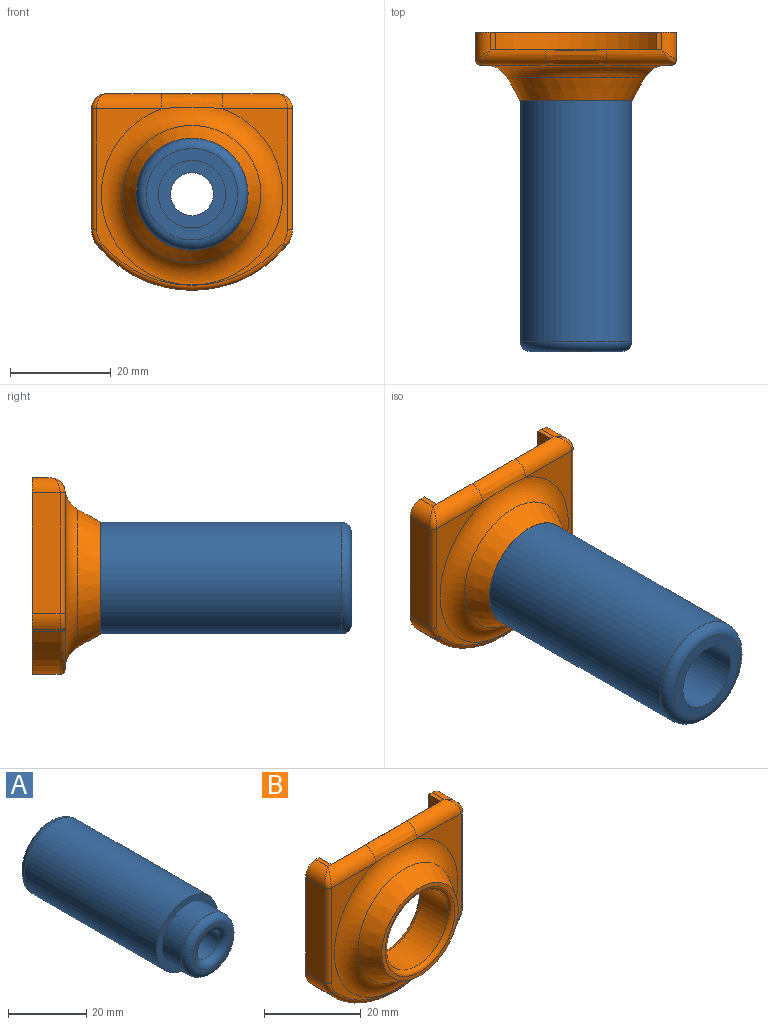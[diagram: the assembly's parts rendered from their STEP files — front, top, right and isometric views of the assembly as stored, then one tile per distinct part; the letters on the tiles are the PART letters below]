
ASSEMBLY  parts=2 mates=1
PART A: 11 faces, bbox 24x59x24 mm
  f0: cylinder r=11.1mm len=48mm, axis (0,-1,0), area 3347.7mm2, adj f7,f10
  f1: plane 14.2x14.2mm, normal (0,-1,0), area 35.6mm2, adj f8,f9
  f2: cylinder r=6.7mm len=34mm, axis (0,-1,0), area 1431.3mm2, adj f3,f4
  f3: plane 18.2x18.2mm, normal (0,1,0), area 119.1mm2, adj f2,f10
  f4: plane 13.4x13.4mm, normal (0,1,0), area 84.3mm2, adj f2,f5
  f5: cylinder r=4.25mm len=23mm, axis (0,1,0), area 614.2mm2, adj f4,f9
  f6: cylinder r=9.1mm len=18.2mm, axis (0,-1,0), area 400.2mm2, adj f7,f8
  f7: plane 22.2x22.2mm, normal (0,-1,0), area 126.9mm2, adj f0,f6
  f8: torus R=7.1mm, axis (0,-1,0), area 165.3mm2, adj f1,f6
  f9: torus R=6.25mm, axis (0,-1,0), area 98.2mm2, adj f1,f5
  f10: torus R=9.1mm, axis (0,-1,0), area 204.8mm2, adj f0,f3
PART B: 46 faces, bbox 46.7x13.5x46.7 mm
  f0: plane 40x39.13mm, normal (0,1,0), area 362.7mm2, adj f1,f4,f5,f6,f7,f8,f9,f10
  f1: plane 3.5x1mm, normal (0,0,1), area 3.5mm2, adj f0,f12,f28,f30
  f2: plane 12.11x0.07mm, normal (0,0,1), area 0.4mm2, adj f15,f31
  f3: plane 22.33x22.33mm, normal (0,-1,0), area 64.6mm2, adj f17,f45
  f4: plane 24.05x5.5mm, normal (1,0,0), area 132.3mm2, adj f0,f10,f25,f34
  f5: plane 24.05x5.5mm, normal (-1,0,0), area 132.3mm2, adj f0,f8,f19,f28
  f6: plane 5.5x0.3mm, normal (-0.76,0,-0.65), area 2.2mm2, adj f0,f8,f9,f21
  f7: plane 5.5x0.3mm, normal (0.76,0,-0.65), area 2.2mm2, adj f0,f9,f10,f23
  f8: cylinder r=5mm len=5.5mm, axis (0,1,0), area 19.5mm2, adj f0,f5,f6,f20
  f9: cylinder r=24.42mm len=37.07mm, axis (0,1,0), area 231.5mm2, adj f0,f6,f7,f22
  f10: cylinder r=5mm len=5.5mm, axis (0,1,0), area 19.5mm2, adj f0,f4,f7,f24
  f11: cylinder r=9.2mm len=18.4mm, axis (0,1,0), area 462.4mm2, adj f26,f45
  f12: plane 27.39x3.5mm, normal (1,0,0), area 95.9mm2, adj f0,f1,f13,f15
  f13: cylinder r=20.42mm len=32mm, axis (0,-1,0), area 128.7mm2, adj f0,f12,f14,f15
  f14: plane 27.39x3.5mm, normal (-1,0,0), area 95.9mm2, adj f0,f13,f15,f27
  f15: plane 35.13x32mm, normal (0,1,0), area 722.2mm2, adj f2,f12,f13,f14,f26,f30,f32
  f16: plane 38x35.13mm, normal (0,-1,0), area 209.1mm2, adj f18,f19,f20,f21,f22,f23,f24,f25
  f17: cone r=15.12mm half-angle=29.6deg, axis (0,1,0), area 401.1mm2, adj f3,f18
  f18: torus R=18.05mm, axis (0,-1,0), area 513.1mm2, adj f16,f17,f31
  f19: cylinder r=1mm len=24.05mm, axis (0,0,1), area 37.8mm2, adj f5,f16,f20,f29
  f20: torus R=4mm, axis (0,-1,0), area 5.2mm2, adj f8,f16,f19,f21
  f21: cylinder r=1mm len=1.02mm, axis (-0.65,0,0.76), area 0.6mm2, adj f6,f16,f20,f22
  f22: torus R=23.42mm, axis (0,-1,0), area 65.1mm2, adj f9,f16,f21,f23
  f23: cylinder r=1mm len=1.02mm, axis (-0.65,0,-0.76), area 0.6mm2, adj f7,f16,f22,f24
  f24: torus R=4mm, axis (0,-1,0), area 5.2mm2, adj f10,f16,f23,f25
  f25: cylinder r=1mm len=24.05mm, axis (0,0,-1), area 37.8mm2, adj f4,f16,f24,f33
  f26: torus R=10.2mm, axis (0,-1,0), area 94.4mm2, adj f11,f15
  f27: plane 3.5x1mm, normal (0,0,1), area 3.5mm2, adj f0,f14,f32,f34
  f28: cylinder r=3mm len=5.5mm, axis (0,1,0), area 22.5mm2, adj f0,f1,f5,f29
  f29: bspline ~3.52x3mm, area 5mm2, adj f19,f28,f30
  f30: cylinder r=3mm len=12.95mm, axis (-1,0,0), area 57.6mm2, adj f1,f15,f16,f29,f31
  f31: bspline ~16.45x3.42mm, area 53.9mm2, adj f2,f18,f30,f32
  f32: cylinder r=3mm len=12.95mm, axis (-1,0,0), area 57.6mm2, adj f15,f16,f27,f31,f33
  f33: bspline ~3.52x3mm, area 5mm2, adj f25,f32,f34
  f34: cylinder r=3mm len=5.5mm, axis (0,-1,0), area 22.5mm2, adj f0,f4,f27,f33
  f35: cylinder r=1.25mm len=4mm, axis (0,1,0), area 31.4mm2, adj f0,f36
  f36: plane 2.5x2.5mm, normal (0,1,0), area 4.9mm2, adj f35
  f37: cylinder r=1.25mm len=4mm, axis (0,1,0), area 31.4mm2, adj f0,f38
  f38: plane 2.5x2.5mm, normal (0,1,0), area 4.9mm2, adj f37
  f39: cylinder r=1.25mm len=4mm, axis (0,1,0), area 31.4mm2, adj f0,f40
  f40: plane 2.5x2.5mm, normal (0,1,0), area 4.9mm2, adj f39
  f41: cylinder r=1.25mm len=4mm, axis (0,1,0), area 31.4mm2, adj f0,f42
  f42: plane 2.5x2.5mm, normal (0,1,0), area 4.9mm2, adj f41
  f43: cylinder r=1.25mm len=4mm, axis (0,1,0), area 31.4mm2, adj f0,f44
  f44: plane 2.5x2.5mm, normal (0,1,0), area 4.9mm2, adj f43
  f45: torus R=10.2mm, axis (0,-1,0), area 94.4mm2, adj f3,f11
PLACE A rot(axis=(1,0,0),180deg) t=(7.54,-18.73,-0.94)mm
PLACE B t=(7.54,7.27,-0.94)mm
MATE fastened A.f6 <-> B.f11  axis (0,1,0) through (7.54,-2.73,-0.94)mm
